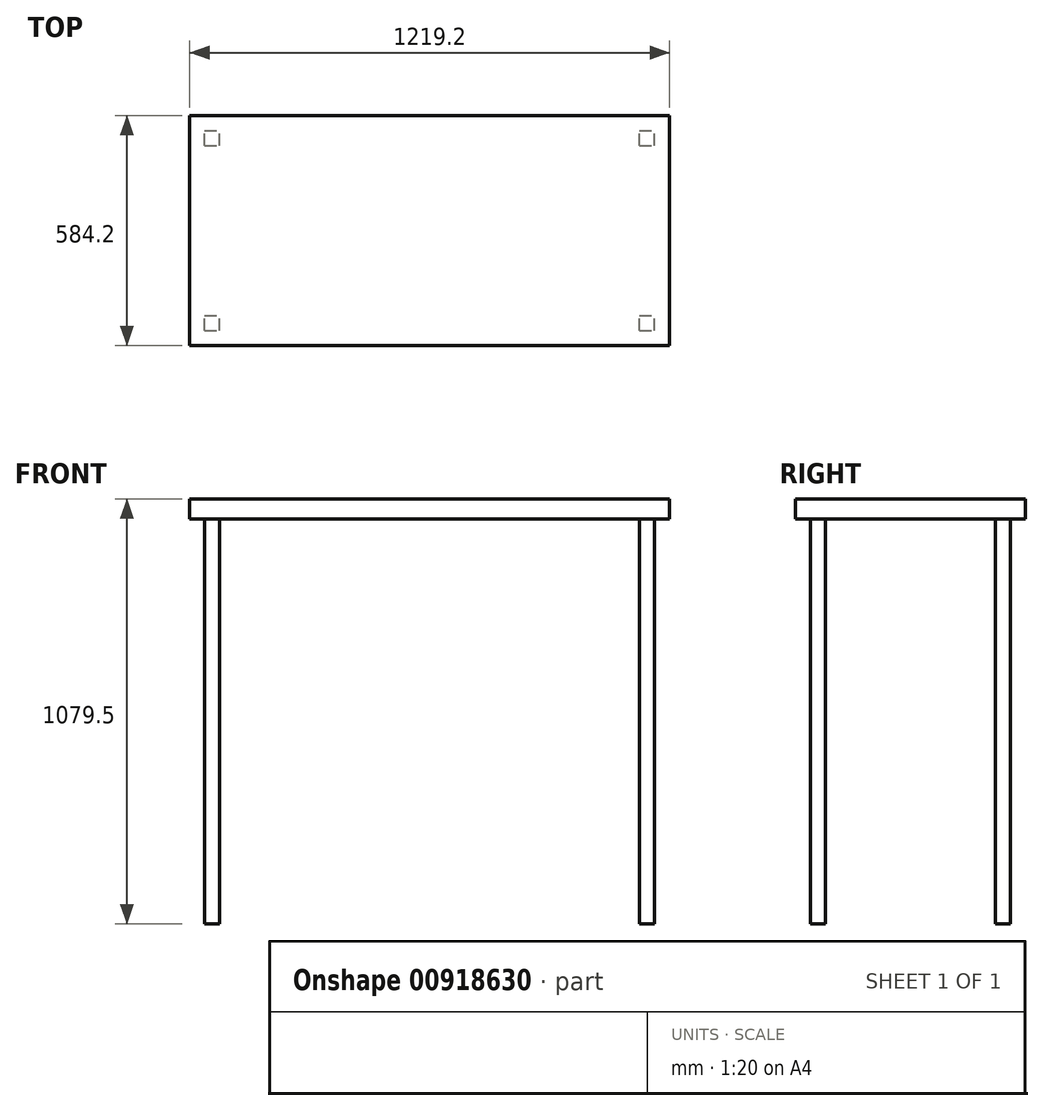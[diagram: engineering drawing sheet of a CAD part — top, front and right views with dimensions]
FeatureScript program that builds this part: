
annotation { "Feature Type Name" : "Feature", "Feature Type Description" : "" }
export const myFeature = defineFeature(function(context is Context, id is Id, definition is map)
    precondition{}
    {
        {
            var Q0;
            Q0=qCreatedBy(makeId("Top.planeOp"),FACE);
            var sketch = newSketch(context, id + "F0", { "sketchPlane" : qUnion([Q0])});
            skLineSegment(sketch, "E0.bottom", {"start": v(-609.6, 292.1) * mm, "end": v(609.6, 292.1) * mm});
            skLineSegment(sketch, "E0.top", {"start": v(-609.6, -292.1) * mm, "end": v(609.6, -292.1) * mm});
            skLineSegment(sketch, "E0.left", {"start": v(-609.6, 292.1) * mm, "end": v(-609.6, -292.1) * mm});
            skLineSegment(sketch, "E0.right", {"start": v(609.6, 292.1) * mm, "end": v(609.6, -292.1) * mm});
            skLineSegment(sketch, "E1", {"start": v(-609.6, 292.1) * mm, "end": v(609.6, -292.1) * mm, "construction": true});
            skSolve(sketch);
        }
        {
            var Q0;
            Q0=makeQuery(id+"F0.imprint","IMPRINT",FACE,{"disambiguationData":[TD([[makeQuery(id+"F0.imprint","IMPRINT",EDGE,{"derivedFrom":sQuery(id+"F0.wireOp",EDGE,"E0.bottom")}),-1.0]])]});
            extrude(context, id + "F1", {"entities" : qUnion([Q0]), "depth" : 50.8 * mm, "offsetDistance" : 25.4 * mm});
        }
        {
            var Q0;
            Q0=makeQuery(id+"F1.opExtrude","CAP_FACE",FACE,{"disambiguationData":[OSD([sQuery(id+"F0.wireOp",EDGE,"E0.bottom"),sQuery(id+"F0.wireOp",EDGE,"E0.top"),sQuery(id+"F0.wireOp",EDGE,"E0.left"),sQuery(id+"F0.wireOp",EDGE,"E0.right")])],"isStart":true});
            var sketch = newSketch(context, id + "F2", { "sketchPlane" : qUnion([Q0])});
            skLineSegment(sketch, "E2.bottom", {"start": v(-571.5, 254) * mm, "end": v(-533.4, 254) * mm});
            skLineSegment(sketch, "E2.top", {"start": v(-571.5, 215.9) * mm, "end": v(-533.4, 215.9) * mm});
            skLineSegment(sketch, "E2.left", {"start": v(-571.5, 254) * mm, "end": v(-571.5, 215.9) * mm});
            skLineSegment(sketch, "E2.right", {"start": v(-533.4, 254) * mm, "end": v(-533.4, 215.9) * mm});
            skLineSegment(sketch, "E3.bottom", {"start": v(-571.5, -215.9) * mm, "end": v(-533.4, -215.9) * mm});
            skLineSegment(sketch, "E3.top", {"start": v(-571.5, -254) * mm, "end": v(-533.4, -254) * mm});
            skLineSegment(sketch, "E3.left", {"start": v(-571.5, -215.9) * mm, "end": v(-571.5, -254) * mm});
            skLineSegment(sketch, "E3.right", {"start": v(-533.4, -215.9) * mm, "end": v(-533.4, -254) * mm});
            skLineSegment(sketch, "E4.bottom", {"start": v(533.4, 254) * mm, "end": v(571.5, 254) * mm});
            skLineSegment(sketch, "E4.top", {"start": v(533.4, 215.9) * mm, "end": v(571.5, 215.9) * mm});
            skLineSegment(sketch, "E4.left", {"start": v(533.4, 254) * mm, "end": v(533.4, 215.9) * mm});
            skLineSegment(sketch, "E4.right", {"start": v(571.5, 254) * mm, "end": v(571.5, 215.9) * mm});
            skLineSegment(sketch, "E5.bottom", {"start": v(533.4, -215.9) * mm, "end": v(571.5, -215.9) * mm});
            skLineSegment(sketch, "E5.top", {"start": v(533.4, -254) * mm, "end": v(571.5, -254) * mm});
            skLineSegment(sketch, "E5.left", {"start": v(533.4, -215.9) * mm, "end": v(533.4, -254) * mm});
            skLineSegment(sketch, "E5.right", {"start": v(571.5, -215.9) * mm, "end": v(571.5, -254) * mm});
            skLineSegment(sketch, "E6", {"start": v(-533.4, 215.9) * mm, "end": v(533.4, -215.9) * mm, "construction": true});
            skLineSegment(sketch, "E7", {"start": v(-533.4, -215.9) * mm, "end": v(533.4, 215.9) * mm, "construction": true});
            skSolve(sketch);
        }
        {
            var Q0;
            Q0=makeQuery(id+"F2.imprint","IMPRINT",FACE,{"disambiguationData":[TD([[makeQuery(id+"F2.imprint","IMPRINT",EDGE,{"derivedFrom":sQuery(id+"F2.wireOp",EDGE,"E2.bottom")}),-1.0]])]});
            var Q1;
            Q1=makeQuery(id+"F2.imprint","IMPRINT",FACE,{"disambiguationData":[TD([[makeQuery(id+"F2.imprint","IMPRINT",EDGE,{"derivedFrom":sQuery(id+"F2.wireOp",EDGE,"E3.bottom")}),-1.0]])]});
            var Q2;
            Q2=makeQuery(id+"F2.imprint","IMPRINT",FACE,{"disambiguationData":[TD([[makeQuery(id+"F2.imprint","IMPRINT",EDGE,{"derivedFrom":sQuery(id+"F2.wireOp",EDGE,"E5.bottom")}),-1.0]])]});
            var Q3;
            Q3=makeQuery(id+"F2.imprint","IMPRINT",FACE,{"disambiguationData":[TD([[makeQuery(id+"F2.imprint","IMPRINT",EDGE,{"derivedFrom":sQuery(id+"F2.wireOp",EDGE,"E4.bottom")}),-1.0]])]});
            extrude(context, id + "F3", {"entities" : qUnion([Q0, Q1, Q2, Q3]), "operationType" : NewBodyOperationType.ADD, "depth" : 1028.7 * mm, "offsetDistance" : 25.4 * mm});
        }
    });
